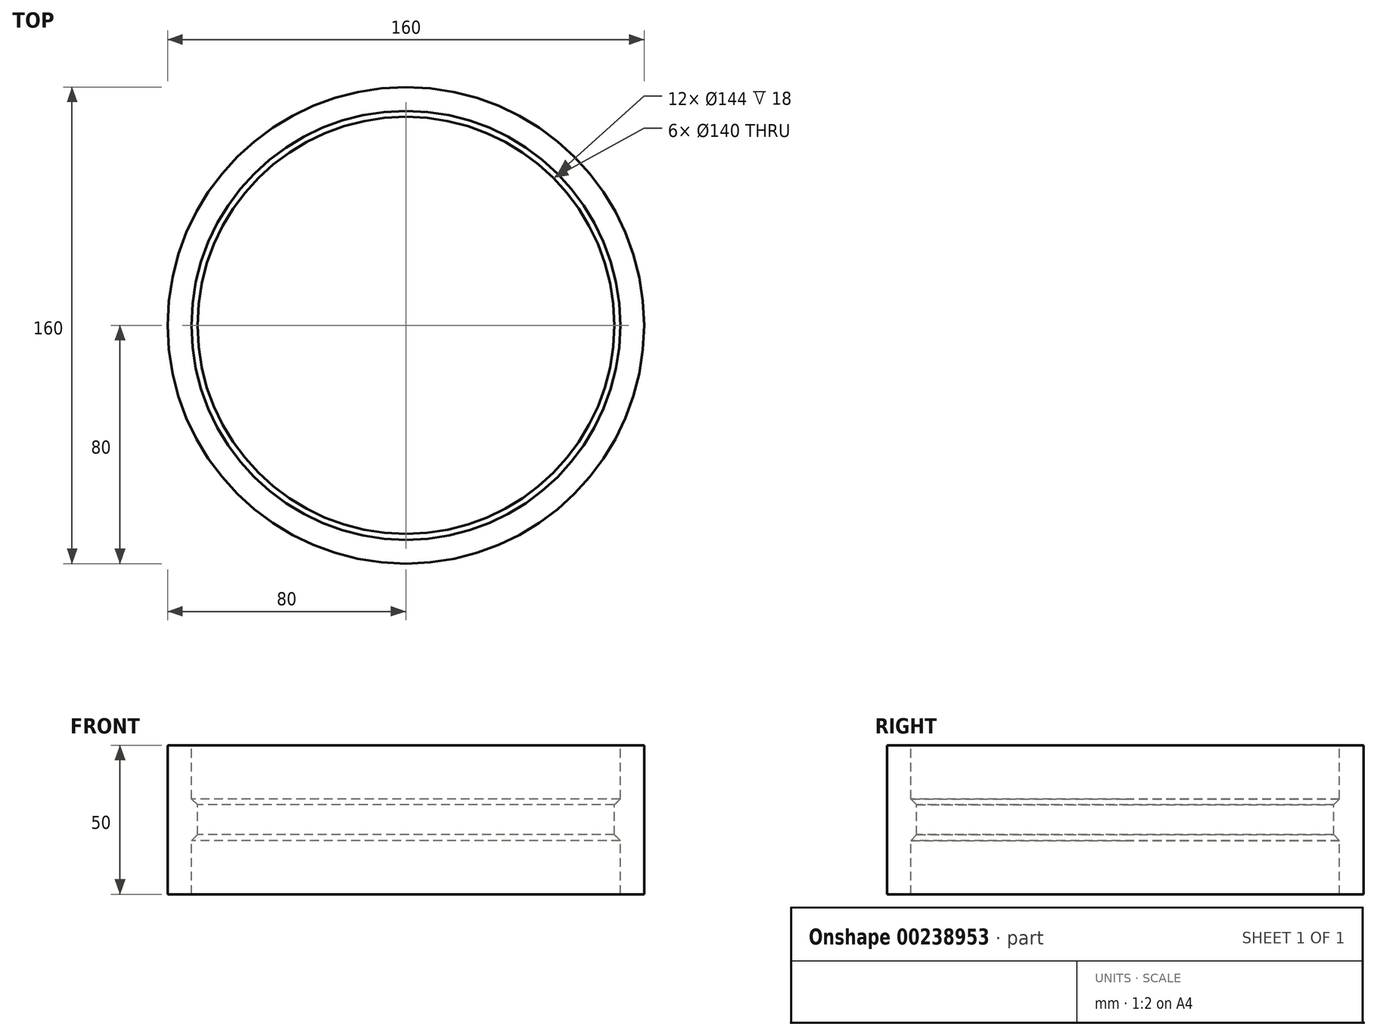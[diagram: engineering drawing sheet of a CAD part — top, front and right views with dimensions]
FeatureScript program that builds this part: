
annotation { "Feature Type Name" : "Feature", "Feature Type Description" : "" }
export const myFeature = defineFeature(function(context is Context, id is Id, definition is map)
    precondition{}
    {
        {
            var Q0;
            Q0=qCreatedBy(makeId("Front.planeOp"),FACE);
            var sketch = newSketch(context, id + "F0", { "sketchPlane" : qUnion([Q0])});
            skLineSegment(sketch, "E0", {"start": v(-80, 25) * mm, "end": v(-80, -25) * mm});
            skLineSegment(sketch, "E1", {"start": v(-72, 25) * mm, "end": v(-80, 25) * mm});
            skLineSegment(sketch, "E2", {"start": v(-72, 25) * mm, "end": v(-72, 7) * mm});
            skLineSegment(sketch, "E3", {"start": v(-70, 5) * mm, "end": v(-70, -5) * mm});
            skLineSegment(sketch, "E4", {"start": v(-80, -25) * mm, "end": v(-72, -25) * mm});
            skLineSegment(sketch, "E5.trimOffspring", {"start": v(-72, -7) * mm, "end": v(-72, -25) * mm});
            skPoint(sketch, "E6.orphan", {"position": v(0, -25) * mm});
            skPoint(sketch, "E7.start.orphan", {"position": v(-30.76, -25) * mm});
            skLineSegment(sketch, "E8", {"start": v(0, 18.56) * mm, "end": v(0, -66.84) * mm});
            skLineSegment(sketch, "E9", {"start": v(-72, 7) * mm, "end": v(-70, 5) * mm});
            skLineSegment(sketch, "E10", {"start": v(-72, -7) * mm, "end": v(-70, -5) * mm});
            skSolve(sketch);
        }
        {
            var Q0;
            Q0=qSketchRegion(id+"F0",true);
            var Q1;
            Q1=sQuery(id+"F0.wireOp",EDGE,"E8");
            revolve(context, id + "F1", {"entities" : qUnion([Q0]), "axis" : qUnion([Q1]), "revolveType" : RevolveType.FULL});
        }
        {
            var Q0;
            Q0=qCreatedBy(makeId("Top.planeOp"),FACE);
            var sketch = newSketch(context, id + "F2", { "sketchPlane" : qUnion([Q0])});
            skLineSegment(sketch, "E11", {"start": v(-19.9, -15) * mm, "end": v(24.27, -15) * mm});
            skPoint(sketch, "E12", {"position": v(0, -15) * mm});
            skSolve(sketch);
        }
    });
